# Revit family: AFX-Rhea-LED_Outdoor_Sconce
name_source: partatom
category: Lighting Fixtures
units: mm (PartAtom-declared; Revit-internal decimal feet)

## family parameters
Cut with Voids When Loaded = No
Host = Face
Light Source = Yes
Part Type = Normal
Room Calculation Point = No
Round Connector Dimension = Use Diameter
Shared = No

## types (4) — shared parameters
Apparent Load = 0 VA
Assembly Code = D5020200
Body Finish = AFX - Black Steel
Cap Finish = AFX - Black Steel
Color Filter = 16777215
Colour Rendering Index = 90
Default Elevation = 48"
Depth = 2 1/8"
Diffuser Finish = AFX - White Acrylic
Dimming Lamp Color Temperature Shift = <None>
Emit Shape Visible in Rendering = No
Emit from Rectangle Length = 4 3/4"
Housing Finish = AFX - Black Steel
Keynote = 12500
Manufacturer = AFX Inc
Power Factor = 1
Product Documentation Link = https://www.afxinc.com
Revit File Built By = https://servex-us.com
Sustainability = https://lamprecycle.org
Tilt Angle = 90.00°
Type Comments = Rhea
URL = https://www.afxinc.com
Voltage = 120 V
Width = 5"

## per-type parameters (varying)
| type | Description | Emit from Rectangle Width | Height | Photometric Web File | Wattage Comments |
| REAW0518LAJUDBK | LED Outdoor Sconce - 18"H x 5"H x 2 1/8"D | 17 1/2" | 18" | REAW0518LAJUDBK_3000K_IES.IES | 20W |
| REAW0524LAJUDBK | LED Outdoor Sconce - 24"H x 5"H x 2 1/8"D | 23 1/2" | 24" | REAW0524LAJUDBK_3000K_IES.IES | 25W |
| REAW0536LAJUDBK | LED Outdoor Sconce - 36"H x 5"H x 2 1/8"D | 35 1/2" | 36" | REAW0536LAJUDBK_3000K_IES.IES | 30W |
| REAW0548LAJUDBK | LED Outdoor Sconce - 48"H x 5"H x 2 1/8"D | 47 1/2" | 48" | REAW0548LAJUDBK_3000K_IES.IES | 40W |

note: column(s) folded — value = type name in every type: Model

## geometry (parser evidence)
native form markers: Sweep x1
no freeform markers — native parametric forms only
